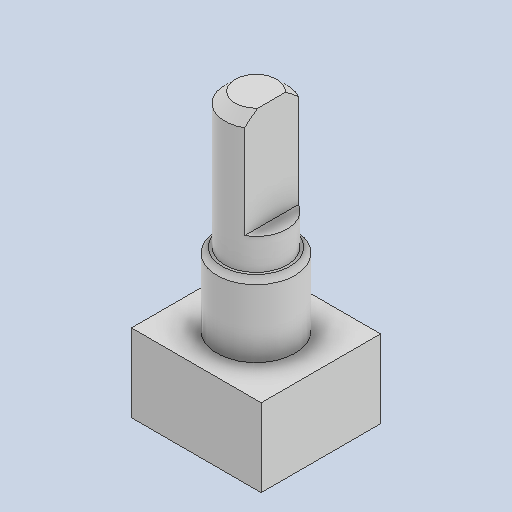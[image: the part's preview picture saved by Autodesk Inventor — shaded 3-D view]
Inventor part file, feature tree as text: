
AUTODESK INVENTOR PART (.ipt)
format: ipt  version: 2025.2 (Build 292293000, 293)  size: 129,024 bytes
history: native  units: mm
features: extrude x4, sketch x4, chamfer x2
ambient origin geometry x8: Origin, YZ Plane, XZ Plane, XY Plane, X Axis, Y Axis, Z Axis, Center Point
bodies: Solid1 (feature_tree)
feature tree (10):
  extrude  "Extrusion1"  Depth=11.5mm
  extrude  "Extrusion2"  Depth=7.5mm
  extrude  "Extrusion3"  Depth=6.0mm
  extrude  "Extrusion4"  Depth=10.0mm
  chamfer  "Chamfer1"  Distance=10.0mm
  chamfer  "Chamfer2"  Distance=0.5mm Angle=45.0deg
  sketch  "Sketch1"  dims[d0=12.5mm d1=11.5mm]
  sketch  "Sketch2"  dims[d2=7.5mm d3=0.0mm d4=7.5mm]
  sketch  "Sketch3"  dims[d5=7.0mm d6=0.0mm d7=6.0mm]
  sketch  "Sketch4"  dims[d8=13.0mm d9=0.0mm d10=4.5mm d11=10.0mm d12=0.0mm d13=0.5mm d14=2.0mm d15=45.0deg d16=1.0mm d17=2.0mm d18=45.0deg]
